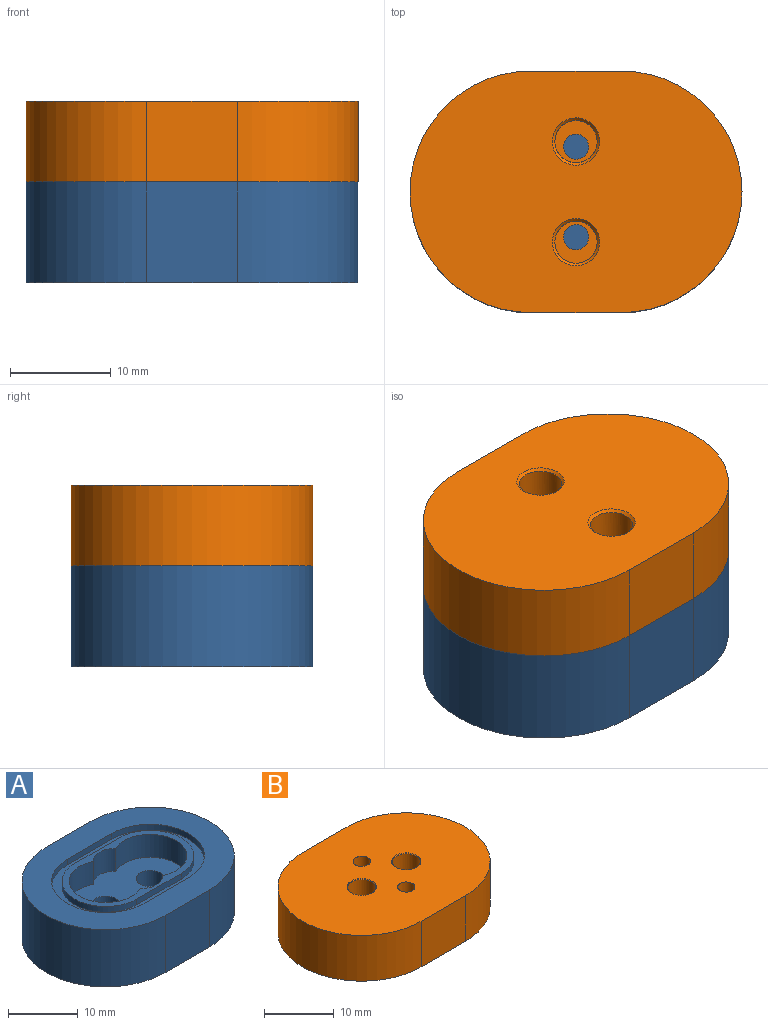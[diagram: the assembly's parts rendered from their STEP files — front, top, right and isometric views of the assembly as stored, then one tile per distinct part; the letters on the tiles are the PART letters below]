
ASSEMBLY  parts=2 mates=1
PART A: 26 faces, bbox 33x24x10 mm
  f0: cylinder r=2mm len=5mm, axis (0,0,1), area 62.8mm2, adj f21,f25
  f1: plane 21.5x12.5mm, normal (0,0,1), area 53.9mm2, adj f8,f9,f10,f15,f17,f18,f19,f20
  f2: plane 10x9mm, normal (0,1,0), area 90mm2, adj f3,f5,f6,f7
  f3: cylinder r=12mm len=24mm, axis (0,0,1), area 377mm2, adj f2,f4,f6,f7
  f4: plane 10x9mm, normal (0,-1,0), area 90mm2, adj f3,f5,f6,f7
  f5: cylinder r=12mm len=24mm, axis (0,0,1), area 377mm2, adj f2,f4,f6,f7
  f6: plane 33x24mm, normal (0,0,-1), area 618.1mm2, adj f2,f3,f4,f5,f24
  f7: plane 33x24mm, normal (0,0,1), area 340.2mm2, adj f2,f3,f4,f5,f11,f12,f13,f14
  f8: cylinder r=6.25mm len=12.5mm, axis (0,0,1), area 19.6mm2, adj f1,f9,f15,f16
  f9: plane 9x1mm, normal (0,1,0), area 9mm2, adj f1,f8,f10,f16
  f10: cylinder r=6.25mm len=12.5mm, axis (0,0,1), area 19.6mm2, adj f1,f9,f15,f16
  f11: cylinder r=7.75mm len=15.5mm, axis (0,0,1), area 24.3mm2, adj f7,f12,f14,f16
  f12: plane 9x1mm, normal (0,1,0), area 9mm2, adj f7,f11,f13,f16
  f13: cylinder r=7.75mm len=15.5mm, axis (0,0,1), area 24.3mm2, adj f7,f12,f14,f16
  f14: plane 9x1mm, normal (0,-1,0), area 9mm2, adj f7,f11,f13,f16
  f15: plane 9x1mm, normal (0,-1,0), area 9mm2, adj f1,f8,f10,f16
  f16: plane 24.5x15.5mm, normal (0,0,1), area 93mm2, adj f8,f9,f10,f11,f12,f13,f14,f15
  f17: cylinder r=3mm len=4.49mm, axis (0,0,1), area 20.3mm2, adj f1,f18,f20,f21
  f18: cylinder r=5.25mm len=10.5mm, axis (0,0,1), area 84.6mm2, adj f1,f17,f19,f21
  f19: cylinder r=3mm len=4.49mm, axis (0,0,1), area 20.3mm2, adj f1,f18,f20,f21
  f20: cylinder r=5.25mm len=10.5mm, axis (0,0,1), area 84.6mm2, adj f1,f17,f19,f21
  f21: plane 19.5x11.5mm, normal (0,0,1), area 156.2mm2, adj f0,f17,f18,f19,f20,f23
  f22: plane 4x4mm, normal (0,0,1), area 12.6mm2, adj f23
  f23: cylinder r=2mm len=4mm, axis (0,0,1), area 50.3mm2, adj f21,f22
  f24: cylinder r=4mm len=8mm, axis (0,0,-1), area 25.1mm2, adj f6,f25
  f25: plane 8x8mm, normal (0,0,-1), area 37.7mm2, adj f0,f24
PART B: 20 faces, bbox 33x24x8 mm
  f0: cylinder r=1.25mm len=2.5mm, axis (0,0,1), area 15.7mm2, adj f7,f13
  f1: cylinder r=1.25mm len=2.5mm, axis (0,0,1), area 15.7mm2, adj f7,f15
  f2: cylinder r=12mm len=24mm, axis (0,0,1), area 301.6mm2, adj f3,f5,f6,f7
  f3: plane 9x8mm, normal (0,-1,0), area 72mm2, adj f2,f4,f6,f7
  f4: cylinder r=12mm len=24mm, axis (0,0,1), area 301.6mm2, adj f3,f5,f6,f7
  f5: plane 9x8mm, normal (0,1,0), area 72mm2, adj f2,f4,f6,f7
  f6: plane 33x24mm, normal (0,0,-1), area 633.7mm2, adj f2,f3,f4,f5,f16,f17
  f7: plane 33x24mm, normal (0,0,1), area 630.9mm2, adj f0,f1,f2,f3,f4,f5,f18,f19
  f8: cylinder r=2mm len=4mm, axis (0,0,1), area 49mm2, adj f9,f18
  f9: plane 4x4mm, normal (0,0,1), area 12.6mm2, adj f8
  f10: cylinder r=2mm len=4mm, axis (0,0,1), area 49mm2, adj f11,f19
  f11: plane 4x4mm, normal (0,0,1), area 12.6mm2, adj f10
  f12: cylinder r=2.1mm len=5.75mm, axis (0,0,-1), area 75.9mm2, adj f13,f16
  f13: plane 4.2x4.2mm, normal (0,0,-1), area 8.9mm2, adj f0,f12
  f14: cylinder r=2.1mm len=5.75mm, axis (0,0,-1), area 75.9mm2, adj f15,f17
  f15: plane 4.2x4.2mm, normal (0,0,-1), area 8.9mm2, adj f1,f14
  f16: cone r=2.1mm half-angle=45deg, axis (0,0,-1), area 4.9mm2, adj f6,f12
  f17: cone r=2.1mm half-angle=45deg, axis (0,0,-1), area 4.9mm2, adj f6,f14
  f18: cone r=2mm half-angle=45deg, axis (0,0,1), area 1.8mm2, adj f7,f8
  f19: cone r=2mm half-angle=45deg, axis (0,0,1), area 1.8mm2, adj f7,f10
PLACE A at identity
PLACE B rot(axis=(1,0,0),180deg) t=(0,-24,0)mm
MATE fastened B.f7 <-> A.f7  axis (0,0,-1) through (12,-24,0)mm
